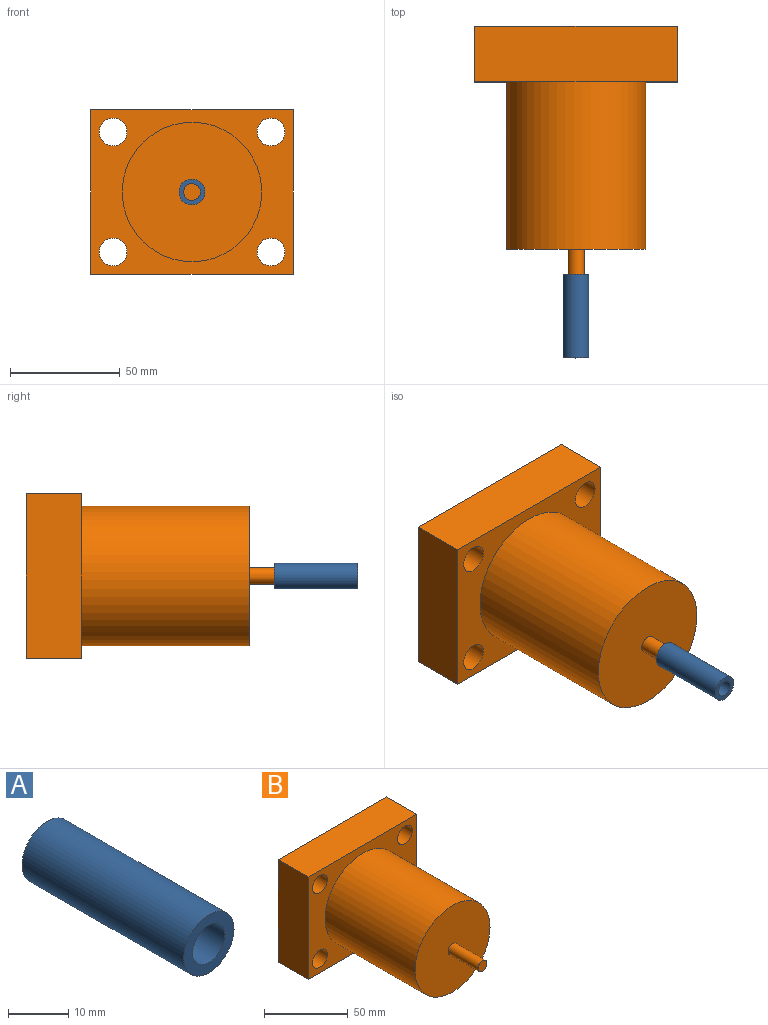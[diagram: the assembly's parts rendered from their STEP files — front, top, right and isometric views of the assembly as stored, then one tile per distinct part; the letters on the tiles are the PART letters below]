
ASSEMBLY  parts=2 mates=2
PART A: 4 faces, bbox 11.8x38.1x11.8 mm
  f0: cylinder r=3.81mm len=38.1mm, axis (0,1,0), area 912.1mm2, adj f2,f3
  f1: cylinder r=5.92mm len=38.1mm, axis (0,1,0), area 1416.3mm2, adj f2,f3
  f2: plane 11.83x11.83mm, normal (0,-1,0), area 64.4mm2, adj f0,f1
  f3: plane 11.83x11.83mm, normal (0,1,0), area 64.4mm2, adj f0,f1
PART B: 14 faces, bbox 92.2x127x75 mm
  f0: plane 75.01x25.4mm, normal (-1,0,0), area 1905.1mm2, adj f1,f7,f8,f9
  f1: plane 92.25x25.4mm, normal (0,0,-1), area 2343.1mm2, adj f0,f2,f8,f9
  f2: plane 75.01x25.4mm, normal (1,0,0), area 1905.1mm2, adj f1,f7,f8,f9
  f3: cylinder r=6.35mm len=25.4mm, axis (0,1,0), area 1013.4mm2, adj f8,f9
  f4: cylinder r=6.35mm len=25.4mm, axis (0,1,0), area 1013.4mm2, adj f8,f9
  f5: cylinder r=6.35mm len=25.4mm, axis (0,1,0), area 1013.4mm2, adj f8,f9
  f6: cylinder r=6.35mm len=25.4mm, axis (0,1,0), area 1013.4mm2, adj f8,f9
  f7: plane 92.25x25.4mm, normal (0,0,1), area 2343.1mm2, adj f0,f2,f8,f9
  f8: plane 92.25x75.01mm, normal (0,-1,0), area 3245.4mm2, adj f0,f1,f2,f3,f4,f5,f6,f7
  f9: plane 92.25x75.01mm, normal (0,1,0), area 6412.3mm2, adj f0,f1,f2,f3,f4,f5,f6,f7
  f10: cylinder r=31.75mm len=76.2mm, axis (0,1,0), area 15201.2mm2, adj f8,f11
  f11: plane 63.5x63.5mm, normal (0,-1,0), area 3121.3mm2, adj f10,f12
  f12: cylinder r=3.81mm len=25.4mm, axis (0,1,0), area 608mm2, adj f11,f13
  f13: plane 7.62x7.62mm, normal (0,-1,0), area 45.6mm2, adj f12
PLACE A t=(-54.67,-118.82,-25.88)mm
PLACE B t=(-54.67,-5.79,-25.88)mm
MATE cylindrical A.f0 <-> B.f10  axis (0,1,0) through (-54.67,-137.87,-25.88)mm
MATE parallel A.f0 <-> B.f10  axis (0,1,0) through (-54.67,-118.82,-25.88)mm
